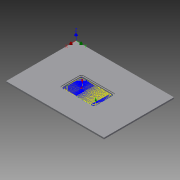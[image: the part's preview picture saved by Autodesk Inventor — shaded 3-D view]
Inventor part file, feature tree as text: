
AUTODESK INVENTOR PART (.ipt)
format: ipt  version: 2015 SP1 (Build 190203100, 203)  size: 430,080 bytes
history: native  units: mm
features: extrude x4, sketch x4, projected_geometry x2, fillet x1
ambient origin geometry x8: Origin, YZ Plane, XZ Plane, XY Plane, X Axis, Y Axis, Z Axis, Center Point
bodies: Solid1 (feature_tree)
feature tree (11):
  extrude  "Extrusion1"  Depth=400.0mm
  extrude  "Extrusion2"  Depth=126.0mm
  fillet  "Fillet1"  Radius=181.25mm
  extrude  "Extrusion3"  Depth=5.0mm
  extrude  "Extrusion4"  Depth=5.0mm
  sketch  "Sketch1"  dims[d0=560.0mm d1=400.0mm]
  sketch  "Sketch2"  dims[d2=8.0mm d3=0.0mm d5=126.0mm d6=181.25mm]
  sketch  "Sketch3"  dims[d7=150.0mm d8=5.0mm]
  projected_geometry  "Projected Loop1"
  sketch  "Sketch4"  dims[d9=5.0mm d10=5.0mm d11=5.0mm d12=4.0mm d13=0.0mm d14=12.0mm d15=4.0mm d16=0.0mm d17=5.0mm d18=5.0mm d19=5.0mm d20=5.0mm d21=12.0mm d22=4.0mm d23=0.0mm]
  projected_geometry  "Projected Loop2"
